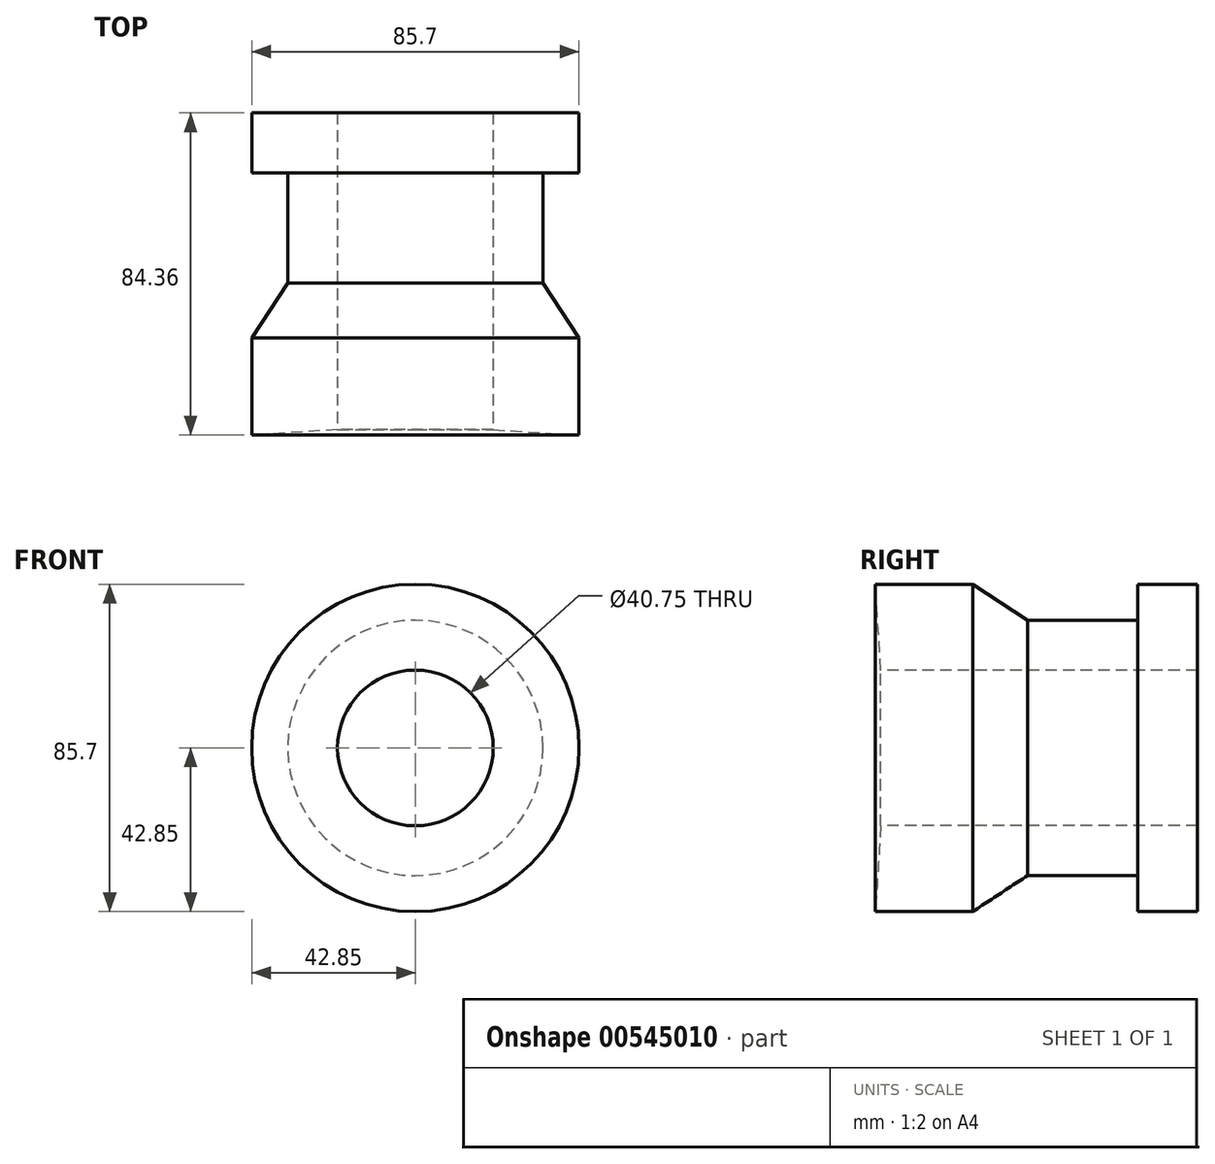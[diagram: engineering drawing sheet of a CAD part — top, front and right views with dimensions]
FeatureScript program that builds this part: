
annotation { "Feature Type Name" : "Feature", "Feature Type Description" : "" }
export const myFeature = defineFeature(function(context is Context, id is Id, definition is map)
    precondition{}
    {
        {
            var Q0;
            Q0=qCreatedBy(makeId("Right.planeOp"),FACE);
            var sketch = newSketch(context, id + "F0", { "sketchPlane" : qUnion([Q0])});
            skLineSegment(sketch, "E0", {"start": v(-38.36, -20.38) * mm, "end": v(44.54, -20.38) * mm});
            skLineSegment(sketch, "E1", {"start": v(44.54, -20.38) * mm, "end": v(44.54, -42.85) * mm});
            skLineSegment(sketch, "E2", {"start": v(44.54, -42.85) * mm, "end": v(28.86, -42.85) * mm});
            skLineSegment(sketch, "E3", {"start": v(28.86, -42.85) * mm, "end": v(28.86, -33.41) * mm});
            skLineSegment(sketch, "E4", {"start": v(28.86, -33.41) * mm, "end": v(0, -33.41) * mm});
            skLineSegment(sketch, "E5", {"start": v(0, -33.41) * mm, "end": v(-14.32, -42.85) * mm});
            skLineSegment(sketch, "E6", {"start": v(-14.32, -42.85) * mm, "end": v(-39.82, -42.85) * mm});
            skLineSegment(sketch, "E7", {"start": v(-39.82, -42.85) * mm, "end": v(-38.36, -20.38) * mm});
            skSolve(sketch);
        }
        {
            var Q0;
            Q0=qCreatedBy(makeId("Right.planeOp"),FACE);
            var sketch = newSketch(context, id + "F1", { "sketchPlane" : qUnion([Q0])});
            skLineSegment(sketch, "E8", {"start": v(-39.38, 0) * mm, "end": v(42.6, 0) * mm});
            skSolve(sketch);
        }
        {
            var Q0;
            Q0 = qSketchRegion(id + "F0", true);
            var Q1;
            Q1=sQuery(id+"F1.wireOp",EDGE,"E8");
            revolve(context, id + "F2", {"entities" : qUnion([Q0]), "axis" : qUnion([Q1]), "revolveType" : RevolveType.FULL});
        }
    });
